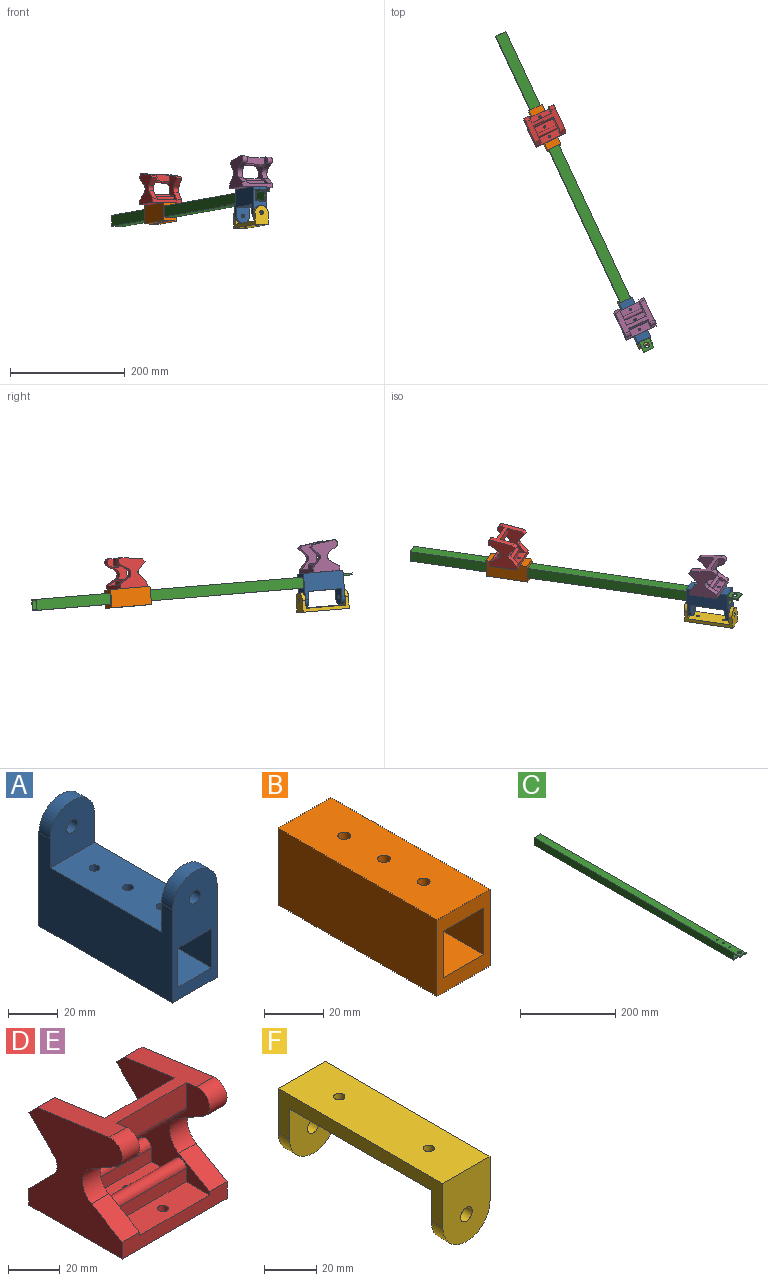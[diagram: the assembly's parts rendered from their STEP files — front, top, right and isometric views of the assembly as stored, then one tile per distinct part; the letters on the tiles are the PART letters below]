
ASSEMBLY  parts=6 mates=12
PART A: 22 faces, bbox 25.4x76.2x58.7 mm
  f0: plane 63.5x25.4mm, normal (0,0,1), area 1569.2mm2, adj f3,f7,f8,f13,f15,f19,f21
  f1: plane 76.2x19.3mm, normal (0,0,-1), area 1427.3mm2, adj f2,f4,f7,f8,f14,f15,f20
  f2: plane 76.2x19.3mm, normal (-1,0,0), area 1471mm2, adj f1,f4,f5,f14
  f3: plane 76.2x46.04mm, normal (1,0,0), area 2600.8mm2, adj f0,f4,f6,f12,f13,f14,f18,f19
  f4: plane 58.74x25.4mm, normal (0,1,0), area 1018.4mm2, adj f1,f2,f3,f5,f6,f11,f12,f20
  f5: plane 76.2x19.3mm, normal (0,0,1), area 1427.3mm2, adj f2,f4,f9,f10,f14,f16,f20
  f6: plane 76.2x25.4mm, normal (0,0,-1), area 1891.8mm2, adj f3,f4,f9,f10,f14,f16,f21
  f7: cylinder r=2.15mm len=6.22mm, axis (0,0,-1), area 84.2mm2, adj f0,f1
  f8: cylinder r=2.15mm len=6.22mm, axis (0,0,-1), area 84.2mm2, adj f0,f1
  f9: cylinder r=2.15mm len=6.22mm, axis (0,0,1), area 84.2mm2, adj f5,f6
  f10: cylinder r=2.15mm len=6.22mm, axis (0,0,1), area 84.2mm2, adj f5,f6
  f11: cylinder r=3.17mm len=6.35mm, axis (0,1,0), area 126.7mm2, adj f4,f13
  f12: cylinder r=12.7mm len=25.4mm, axis (0,1,0), area 253.4mm2, adj f3,f4,f13,f21
  f13: plane 26.99x25.4mm, normal (0,-1,0), area 584.6mm2, adj f0,f3,f11,f12,f21
  f14: plane 58.74x25.4mm, normal (0,-1,0), area 1018.4mm2, adj f1,f2,f3,f5,f6,f17,f18,f20
  f15: cylinder r=2.15mm len=6.22mm, axis (0,0,-1), area 84.2mm2, adj f0,f1
  f16: cylinder r=2.15mm len=6.22mm, axis (0,0,1), area 84.2mm2, adj f5,f6
  f17: cylinder r=3.17mm len=6.35mm, axis (0,-1,0), area 126.7mm2, adj f14,f19
  f18: cylinder r=12.7mm len=25.4mm, axis (0,-1,0), area 253.4mm2, adj f3,f14,f19,f21
  f19: plane 26.99x25.4mm, normal (0,1,0), area 584.6mm2, adj f0,f3,f17,f18,f21
  f20: plane 76.2x19.3mm, normal (1,0,0), area 1471mm2, adj f1,f4,f5,f14
  f21: plane 76.2x46.04mm, normal (-1,0,0), area 2600.8mm2, adj f0,f4,f6,f12,f13,f14,f18,f19
PART B: 19 faces, bbox 25.4x76.2x31.8 mm
  f0: plane 76.2x19.3mm, normal (0,0,-1), area 1275mm2, adj f1,f4,f8,f10,f13,f15,f17
  f1: plane 76.2x19.3mm, normal (-1,0,0), area 1471mm2, adj f0,f4,f5,f13
  f2: plane 76.2x31.75mm, normal (1,0,0), area 2419.3mm2, adj f3,f4,f6,f13
  f3: plane 76.2x25.4mm, normal (0,0,1), area 1891.8mm2, adj f2,f4,f7,f9,f13,f14,f18
  f4: plane 31.75x25.4mm, normal (0,1,0), area 433.8mm2, adj f0,f1,f2,f3,f5,f6,f17,f18
  f5: plane 76.2x19.3mm, normal (0,0,1), area 1257.2mm2, adj f1,f4,f11,f12,f13,f16,f17
  f6: plane 76.2x25.4mm, normal (0,0,-1), area 1721.7mm2, adj f2,f4,f11,f12,f13,f16,f18
  f7: cylinder r=2.15mm len=4.31mm, axis (0,0,-1), area 46.7mm2, adj f3,f8
  f8: cone r=2.15mm half-angle=41deg, axis (0,0,-1), area 77.4mm2, adj f0,f7
  f9: cylinder r=2.15mm len=4.31mm, axis (0,0,-1), area 46.7mm2, adj f3,f10
  f10: cone r=2.15mm half-angle=41deg, axis (0,0,-1), area 77.4mm2, adj f0,f9
  f11: cylinder r=4.76mm len=9.53mm, axis (0,0,1), area 186.2mm2, adj f5,f6
  f12: cylinder r=4.76mm len=9.53mm, axis (0,0,1), area 186.2mm2, adj f5,f6
  f13: plane 31.75x25.4mm, normal (0,-1,0), area 433.8mm2, adj f0,f1,f2,f3,f5,f6,f17,f18
  f14: cylinder r=2.15mm len=4.31mm, axis (0,0,-1), area 46.7mm2, adj f3,f15
  f15: cone r=2.15mm half-angle=41deg, axis (0,0,-1), area 77.4mm2, adj f0,f14
  f16: cylinder r=4.76mm len=9.53mm, axis (0,0,1), area 186.2mm2, adj f5,f6
  f17: plane 76.2x19.3mm, normal (1,0,0), area 1471mm2, adj f0,f4,f5,f13
  f18: plane 76.2x31.75mm, normal (-1,0,0), area 2419.3mm2, adj f3,f4,f6,f13
PART C: 22 faces, bbox 19.1x609.6x19.1 mm
  f0: plane 590.55x19.05mm, normal (0,0,-1), area 11212.9mm2, adj f1,f5,f9,f10,f19,f20,f21
  f1: plane 609.6x19.05mm, normal (1,0,0), area 11312.6mm2, adj f0,f6,f7,f9,f10,f11,f13
  f2: plane 609.6x15.88mm, normal (-1,0,0), area 9407.4mm2, adj f3,f6,f8,f9,f10,f11,f13
  f3: plane 590.55x15.88mm, normal (0,0,1), area 9337.9mm2, adj f2,f4,f9,f10,f19,f20,f21
  f4: plane 609.6x15.88mm, normal (1,0,0), area 9407.4mm2, adj f3,f6,f8,f9,f10,f12,f14
  f5: plane 609.6x19.05mm, normal (-1,0,0), area 11312.6mm2, adj f0,f6,f7,f9,f10,f12,f14
  f6: plane 19.05x3.18mm, normal (0,-1,0), area 35.3mm2, adj f1,f2,f4,f5,f7,f8,f13,f14
  f7: plane 609.6x19.05mm, normal (0,0,1), area 11504.5mm2, adj f1,f5,f6,f9,f15,f16,f17,f18
  f8: plane 609.6x15.88mm, normal (0,0,-1), area 9569mm2, adj f2,f4,f6,f9,f15,f16,f17,f18
  f9: plane 19.05x19.05mm, normal (0,1,0), area 110.9mm2, adj f0,f1,f2,f3,f4,f5,f7,f8
  f10: plane 19.05x12.7mm, normal (0,-1,0), area 65.5mm2, adj f0,f1,f2,f3,f4,f5,f11,f12
  f11: cylinder r=3.17mm len=3.18mm, axis (1,0,0), area 7.9mm2, adj f1,f2,f10,f13
  f12: cylinder r=3.17mm len=3.18mm, axis (1,0,0), area 7.9mm2, adj f4,f5,f10,f14
  f13: plane 15.88x1.59mm, normal (0,0,-1), area 25.2mm2, adj f1,f2,f6,f11
  f14: plane 15.88x1.59mm, normal (0,0,-1), area 25.2mm2, adj f4,f5,f6,f12
  f15: cylinder r=1.98mm len=3.97mm, axis (0,0,1), area 19.8mm2, adj f7,f8
  f16: cylinder r=1.98mm len=3.97mm, axis (0,0,1), area 19.8mm2, adj f7,f8
  f17: cylinder r=1.98mm len=3.97mm, axis (0,0,1), area 19.8mm2, adj f7,f8
  f18: cylinder r=4.76mm len=9.53mm, axis (0,0,1), area 47.5mm2, adj f7,f8
  f19: cylinder r=1.98mm len=3.97mm, axis (0,0,1), area 19.8mm2, adj f0,f3
  f20: cylinder r=1.98mm len=3.97mm, axis (0,0,1), area 19.8mm2, adj f0,f3
  f21: cylinder r=1.98mm len=3.97mm, axis (0,0,1), area 19.8mm2, adj f0,f3
PART D: 39 faces, bbox 57.2x50.8x53.9 mm
  f0: plane 38.1x12.7mm, normal (0,0,1), area 470.2mm2, adj f1,f5,f17,f23,f29
  f1: plane 50.8x47.52mm, normal (-1,0,0), area 1248.7mm2, adj f0,f2,f3,f4,f5,f7,f8,f9
  f2: plane 38.1x12.7mm, normal (0,0,1), area 470.2mm2, adj f1,f18,f20,f24,f29
  f3: cylinder r=9.53mm len=16.5mm, axis (-1,0,0), area 190mm2, adj f1,f4,f14,f15
  f4: plane 16.82x9.71mm, normal (0,-0.5,0.87), area 185mm2, adj f1,f3,f5,f15
  f5: plane 57.15x7.94mm, normal (0,-1,0), area 393.1mm2, adj f0,f1,f4,f6,f15,f29,f31,f38
  f6: plane 57.15x50.8mm, normal (0,0,-1), area 2862.3mm2, adj f5,f7,f15,f17,f18,f19,f38
  f7: plane 57.15x7.94mm, normal (0,1,0), area 393.1mm2, adj f1,f6,f8,f15,f16,f29,f32,f38
  f8: plane 13.47x13.47mm, normal (0,0.71,0.71), area 181.5mm2, adj f1,f7,f9,f15
  f9: cylinder r=6.35mm len=9.53mm, axis (-1,0,0), area 95mm2, adj f1,f8,f10,f15
  f10: plane 13.47x13.47mm, normal (0,0.71,-0.71), area 181.5mm2, adj f1,f9,f11,f15
  f11: plane 9.53x4.49mm, normal (0,0.71,0.71), area 60.5mm2, adj f1,f10,f12,f15
  f12: plane 57.15x39.08mm, normal (0,0.14,0.99), area 996mm2, adj f1,f11,f13,f15,f26,f28,f29,f35
  f13: cylinder r=6.35mm len=11.85mm, axis (-1,0,0), area 166.7mm2, adj f1,f12,f14,f15
  f14: plane 13.65x9.53mm, normal (0,-0.5,-0.87), area 150.1mm2, adj f1,f3,f13,f15
  f15: plane 53.87x50.8mm, normal (1,0,0), area 1771.4mm2, adj f3,f4,f5,f6,f7,f8,f9,f10
  f16: plane 38.1x12.7mm, normal (0,0,1), area 470.2mm2, adj f1,f7,f19,f21,f29
  f17: cylinder r=2.08mm len=6.35mm, axis (0,0,1), area 83.1mm2, adj f0,f6
  f18: cylinder r=2.08mm len=6.35mm, axis (0,0,1), area 83.1mm2, adj f2,f6
  f19: cylinder r=2.08mm len=6.35mm, axis (0,0,1), area 83.1mm2, adj f6,f16
  f20: plane 38.1x6.35mm, normal (0,-1,0), area 241.9mm2, adj f1,f2,f22,f29
  f21: plane 38.1x6.35mm, normal (0,1,0), area 241.9mm2, adj f1,f16,f22,f29
  f22: cylinder r=3.17mm len=38.1mm, axis (1,0,0), area 380mm2, adj f1,f20,f21,f29
  f23: plane 38.1x6.35mm, normal (0,-1,0), area 241.9mm2, adj f0,f1,f25,f29
  f24: plane 38.1x6.35mm, normal (0,1,0), area 241.9mm2, adj f1,f2,f25,f29
  f25: cylinder r=3.17mm len=38.1mm, axis (1,0,0), area 380mm2, adj f1,f23,f24,f29
  f26: plane 38.1x10.89mm, normal (0,1,0), area 414.7mm2, adj f1,f12,f27,f29
  f27: cylinder r=3.17mm len=38.1mm, axis (1,0,0), area 380mm2, adj f1,f26,f28,f29
  f28: plane 38.1x11.77mm, normal (0,-1,0), area 448.6mm2, adj f1,f12,f27,f29
  f29: plane 50.8x47.52mm, normal (1,0,0), area 1248.7mm2, adj f0,f2,f5,f7,f12,f16,f20,f21
  f30: cylinder r=9.53mm len=16.5mm, axis (1,0,0), area 190mm2, adj f29,f31,f37,f38
  f31: plane 16.82x9.71mm, normal (0,-0.5,0.87), area 185mm2, adj f5,f29,f30,f38
  f32: plane 13.47x13.47mm, normal (0,0.71,0.71), area 181.5mm2, adj f7,f29,f33,f38
  f33: cylinder r=6.35mm len=9.53mm, axis (1,0,0), area 95mm2, adj f29,f32,f34,f38
  f34: plane 13.47x13.47mm, normal (0,0.71,-0.71), area 181.5mm2, adj f29,f33,f35,f38
  f35: plane 9.53x4.49mm, normal (0,0.71,0.71), area 60.5mm2, adj f12,f29,f34,f38
  f36: cylinder r=6.35mm len=11.85mm, axis (1,0,0), area 166.7mm2, adj f12,f29,f37,f38
  f37: plane 13.65x9.53mm, normal (0,-0.5,-0.87), area 150.1mm2, adj f29,f30,f36,f38
  f38: plane 53.87x50.8mm, normal (-1,0,0), area 1771.4mm2, adj f5,f6,f7,f12,f30,f31,f32,f33
PART E: same geometry as D
PART F: 14 faces, bbox 25.4x88.9x33.3 mm
  f0: plane 88.9x25.4mm, normal (0,0,1), area 2228.9mm2, adj f1,f5,f7,f8,f12,f13
  f1: plane 88.9x20.64mm, normal (-1,0,0), area 746mm2, adj f0,f2,f4,f5,f6,f9,f11,f12
  f2: cylinder r=12.7mm len=25.4mm, axis (0,-1,0), area 253.4mm2, adj f1,f4,f5,f8
  f3: cylinder r=3.17mm len=6.35mm, axis (0,-1,0), area 126.7mm2, adj f4,f5
  f4: plane 26.99x25.4mm, normal (0,1,0), area 584.6mm2, adj f1,f2,f3,f6,f8
  f5: plane 33.34x25.4mm, normal (0,-1,0), area 745.9mm2, adj f0,f1,f2,f3,f8
  f6: plane 76.2x25.4mm, normal (0,0,-1), area 1906.4mm2, adj f1,f4,f7,f8,f11,f13
  f7: cylinder r=2.15mm len=6.35mm, axis (0,0,1), area 85.9mm2, adj f0,f6
  f8: plane 88.9x20.64mm, normal (1,0,0), area 746mm2, adj f0,f2,f4,f5,f6,f9,f11,f12
  f9: cylinder r=12.7mm len=25.4mm, axis (0,1,0), area 253.4mm2, adj f1,f8,f11,f12
  f10: cylinder r=3.17mm len=6.35mm, axis (0,1,0), area 126.7mm2, adj f11,f12
  f11: plane 26.99x25.4mm, normal (0,-1,0), area 584.6mm2, adj f1,f6,f8,f9,f10
  f12: plane 33.34x25.4mm, normal (0,1,0), area 745.9mm2, adj f0,f1,f8,f9,f10
  f13: cylinder r=2.15mm len=6.35mm, axis (0,0,1), area 85.9mm2, adj f0,f6
PLACE A rot(axis=(0.22,-0.98,0.04),178.5deg) t=(95.65,228.23,226.31)mm
PLACE B rot(axis=(-0.19,0.06,0.98),25.5deg) t=(-61.51,564.12,198.24)mm
PLACE C rot(axis=(-0.19,0.06,0.98),25.5deg) t=(119.82,176.64,230.75)mm
PLACE D rot(axis=(-0.01,-0.04,-1),155deg) t=(-58.05,561.02,240.41)mm
PLACE E rot(axis=(-0.19,0.06,0.98),25.5deg) t=(92.82,238.58,267.37)mm
PLACE F rot(axis=(-0.22,0.98,-0.04),179.1deg) t=(114.67,184.5,185.37)mm
MATE parallel A.f21 <-> C.f1  axis (0.91,0.42,-0.04) through (107.14,233.44,224.16)mm
MATE planar C.f7 <-> B.f7  axis (0.01,0.09,1) through (-10.12,455.08,217.04)mm
MATE planar A.f14 <-> F.f4  axis (0.42,-0.9,0.08) through (111.64,192.43,213.14)mm
MATE planar C.f5 <-> B.f17  axis (-0.91,-0.42,0.04) through (-21.03,454.95,207.61)mm
MATE planar B.f14 <-> D.f18  axis (0.01,0.09,1) through (-53.33,548.29,215.49)mm
MATE cylindrical E.f19 <-> A.f8  axis (0.01,0.09,1) through (87.76,247.37,247.02)mm
MATE planar A.f15 <-> C.f7  axis (-0.01,-0.09,-1) through (103.78,211.87,237.37)mm
MATE planar A.f6 <-> E.f18  axis (0.01,0.09,1) through (79.66,264.02,239.25)mm
MATE cylindrical A.f15 <-> C.f15  axis (-0.01,-0.09,-1) through (103.8,212.14,240.47)mm
MATE cylindrical E.f17 <-> A.f15  axis (0.01,0.09,1) through (103.85,212.69,246.73)mm
MATE cylindrical A.f11 <-> F.f3  axis (0.42,-0.9,0.08) through (110.19,194.08,198.9)mm
MATE cylindrical B.f7 <-> D.f18  axis (-0.01,-0.09,-1) through (-61.39,565.49,214.05)mm
